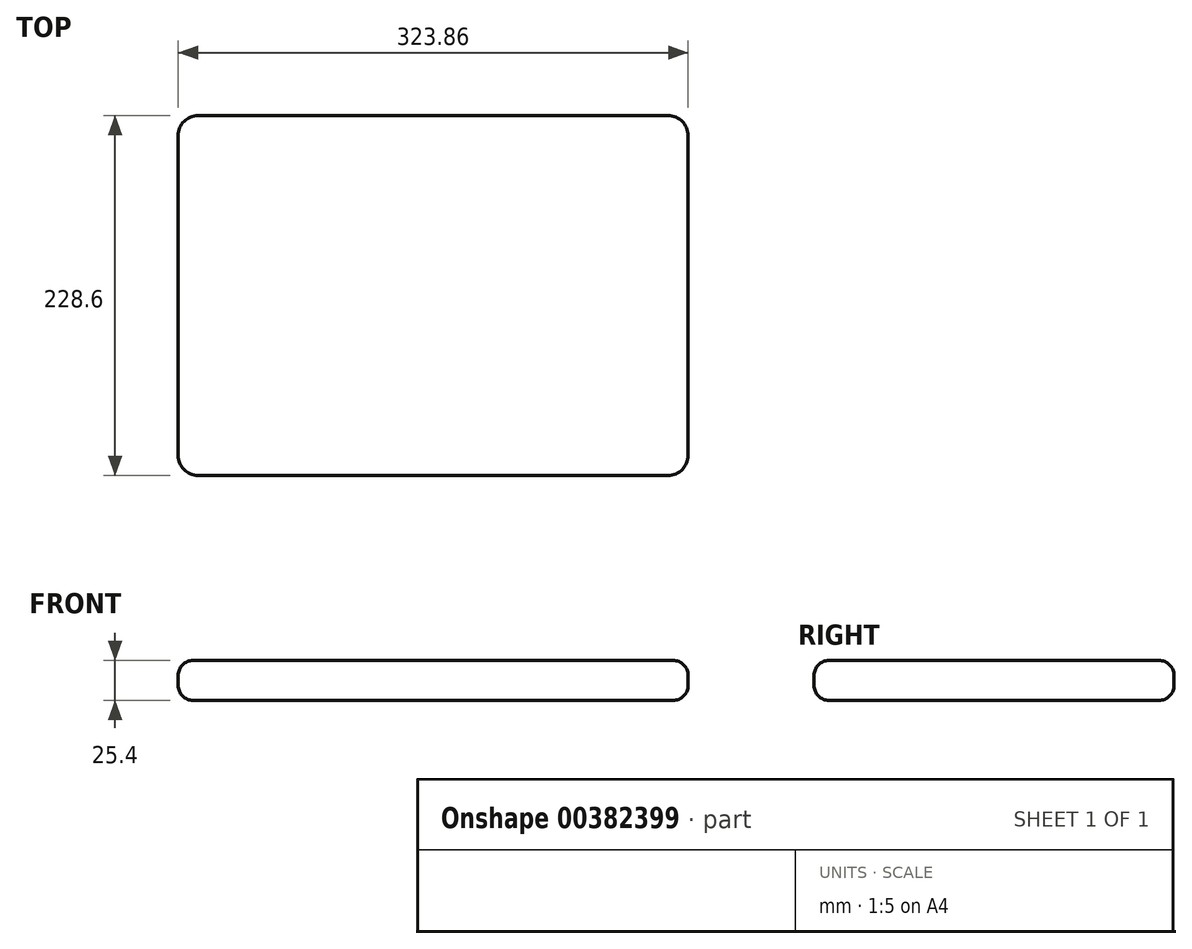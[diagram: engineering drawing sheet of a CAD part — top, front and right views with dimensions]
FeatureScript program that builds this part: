
annotation { "Feature Type Name" : "Feature", "Feature Type Description" : "" }
export const myFeature = defineFeature(function(context is Context, id is Id, definition is map)
    precondition{}
    {
        {
            var Q0;
            Q0=qCreatedBy(makeId("Top.planeOp"),FACE);
            var sketch = newSketch(context, id + "F0", { "sketchPlane" : qUnion([Q0])});
            skLineSegment(sketch, "E0.bottom", {"start": v(-161.93, 114.3) * mm, "end": v(161.93, 114.3) * mm});
            skLineSegment(sketch, "E0.top", {"start": v(-161.93, -114.3) * mm, "end": v(161.93, -114.3) * mm});
            skLineSegment(sketch, "E0.left", {"start": v(-161.92, 114.3) * mm, "end": v(-161.93, -114.3) * mm});
            skLineSegment(sketch, "E0.right", {"start": v(161.93, 114.3) * mm, "end": v(161.92, -114.3) * mm});
            skSolve(sketch);
        }
        {
            var Q0;
            Q0=makeQuery(id+"F0.imprint","IMPRINT",FACE,{"disambiguationData":[TD([[makeQuery(id+"F0.imprint","IMPRINT",EDGE,{"derivedFrom":sQuery(id+"F0.wireOp",EDGE,"E0.bottom")}),-1.0]])]});
            extrude(context, id + "F1", {"entities" : qUnion([Q0]), "depth" : 25.4 * mm});
        }
        {
            var Q0;
            Q0=makeQuery(id+"F1.opExtrude","SWEPT_EDGE",EDGE,{"disambiguationData":[OSD([sQuery(id+"F0.wireOp",EDGE,"E0.top"),sQuery(id+"F0.wireOp",EDGE,"E0.left")])]});
            var Q1;
            Q1=makeQuery(id+"F1.opExtrude","SWEPT_EDGE",EDGE,{"disambiguationData":[OSD([sQuery(id+"F0.wireOp",EDGE,"E0.top"),sQuery(id+"F0.wireOp",EDGE,"E0.right")])]});
            var Q2;
            Q2=makeQuery(id+"F1.opExtrude","SWEPT_EDGE",EDGE,{"disambiguationData":[OSD([sQuery(id+"F0.wireOp",EDGE,"E0.bottom"),sQuery(id+"F0.wireOp",EDGE,"E0.right")])]});
            var Q3;
            Q3=makeQuery(id+"F1.opExtrude","SWEPT_EDGE",EDGE,{"disambiguationData":[OSD([sQuery(id+"F0.wireOp",EDGE,"E0.bottom"),sQuery(id+"F0.wireOp",EDGE,"E0.left")])]});
            fillet(context, id + "F2", {"entities" : qUnion([Q0, Q1, Q2, Q3]), "radius" : 12.7 * mm, "tangentPropagation" : true, "allowEdgeOverflow" : false});
        }
        {
            var Q0;
            Q0=makeQuery(id+"F1.opExtrude","CAP_EDGE",EDGE,{"disambiguationData":[OSD([sQuery(id+"F0.wireOp",EDGE,"E0.bottom")])],"isStart":false});
            var Q1;
            Q1=makeQuery(id+"F1.opExtrude","CAP_EDGE",EDGE,{"disambiguationData":[OSD([sQuery(id+"F0.wireOp",EDGE,"E0.left")])],"isStart":true});
            fillet(context, id + "F3", {"entities" : qUnion([Q0, Q1]), "radius" : 9.52 * mm, "tangentPropagation" : true, "allowEdgeOverflow" : false});
        }
    });
